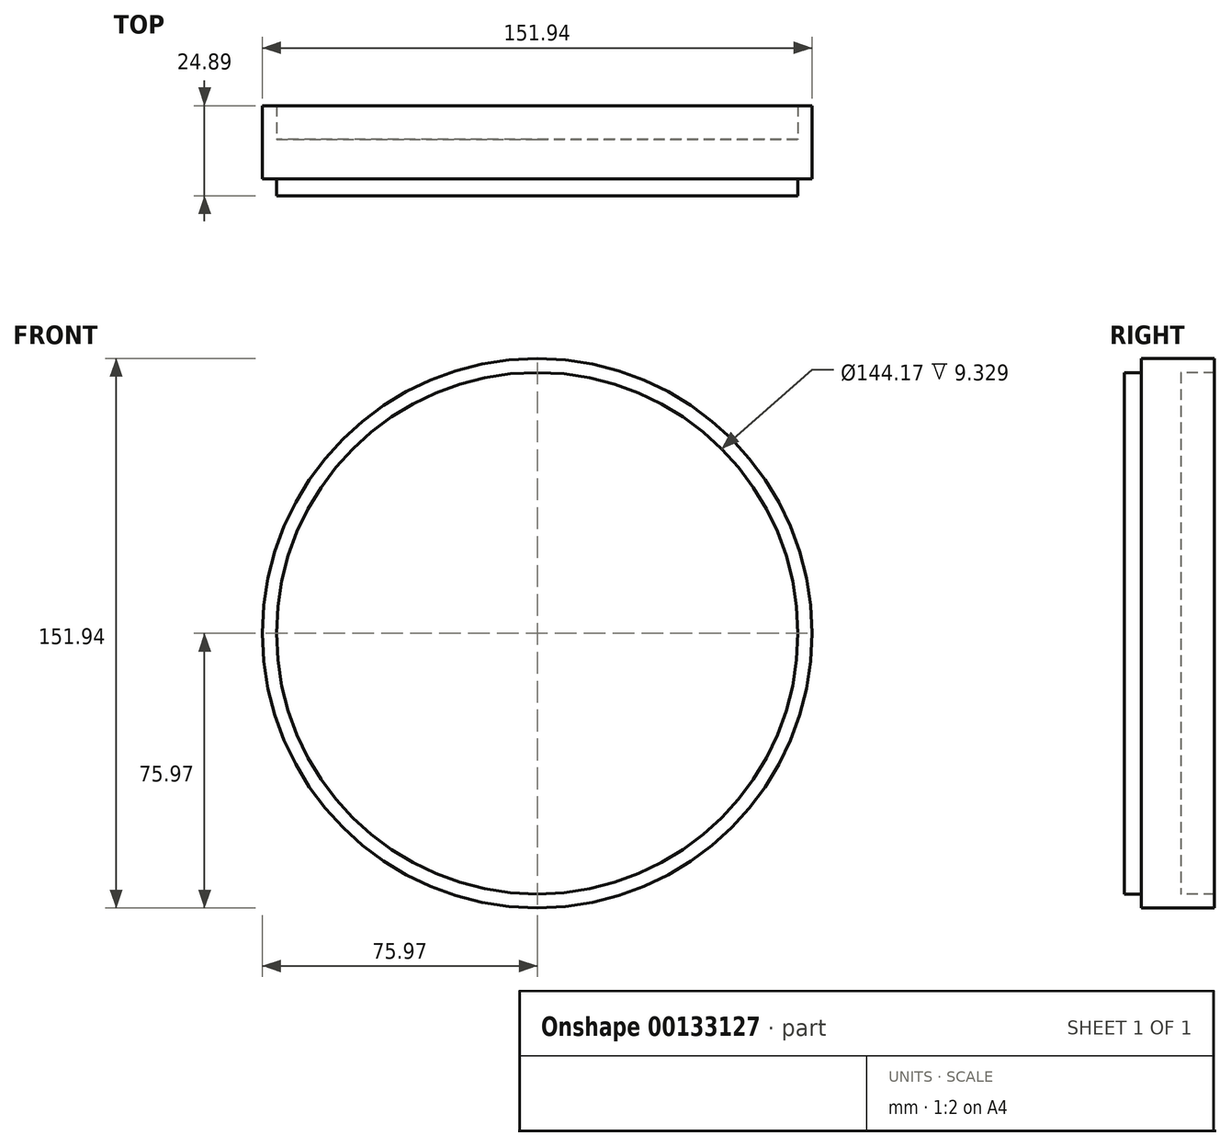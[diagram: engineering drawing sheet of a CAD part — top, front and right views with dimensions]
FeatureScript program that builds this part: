
annotation { "Feature Type Name" : "Feature", "Feature Type Description" : "" }
export const myFeature = defineFeature(function(context is Context, id is Id, definition is map)
    precondition{}
    {
        {
            var Q0;
            Q0=qCreatedBy(makeId("Front.planeOp"),FACE);
            var sketch = newSketch(context, id + "F0", { "sketchPlane" : qUnion([Q0])});
            skCircle(sketch, "E0", {"center": v(0, 0) * mm, "radius": 75.97 * mm});
            skCircle(sketch, "E1", {"center": v(0, 0) * mm, "radius": 70.64 * mm});
            skSolve(sketch);
        }
        {
            var Q0;
            Q0=makeQuery(id+"F0.imprint","IMPRINT",FACE,{"disambiguationData":[TD([[makeQuery(id+"F0.imprint","IMPRINT",EDGE,{"derivedFrom":sQuery(id+"F0.wireOp",EDGE,"E0")}),1.0]])]});
            extrude(context, id + "F1", {"entities" : qUnion([Q0]), "depth" : 10.9 * mm});
        }
        {
            var Q0;
            Q0=qCreatedBy(makeId("Front.planeOp"),FACE);
            var sketch = newSketch(context, id + "F2", { "sketchPlane" : qUnion([Q0])});
            skCircle(sketch, "E2", {"center": v(0, 0) * mm, "radius": 72.1 * mm});
            skSolve(sketch);
        }
        {
            var Q0;
            Q0=makeQuery(id+"F2.imprint","IMPRINT",FACE,{"disambiguationData":[TD([[makeQuery(id+"F2.imprint","IMPRINT",EDGE,{"derivedFrom":sQuery(id+"F2.wireOp",EDGE,"E2")}),1.0]])]});
            extrude(context, id + "F3", {"entities" : qUnion([Q0]), "operationType" : NewBodyOperationType.ADD, "depth" : 15.56 * mm});
        }
        {
            var Q0;
            Q0=makeQuery(id+"F3.boolean.opBoolean","MERGE",FACE,{"derivedFrom":[makeQuery(id+"F1.opExtrude","CAP_FACE",FACE,{"disambiguationData":[OSD([sQuery(id+"F0.wireOp",EDGE,"E0"),sQuery(id+"F0.wireOp",EDGE,"E1")])],"isStart":true}),makeQuery(id+"F3.opExtrude","CAP_FACE",FACE,{"disambiguationData":[OSD([sQuery(id+"F2.wireOp",EDGE,"E2")])],"isStart":true})]});
            var sketch = newSketch(context, id + "F4", { "sketchPlane" : qUnion([Q0])});
            skCircle(sketch, "E3", {"center": v(0, 0) * mm, "radius": 72.09 * mm});
            skSolve(sketch);
        }
        {
            var Q0;
            Q0=makeQuery(id+"F4.imprint","IMPRINT",FACE,{"disambiguationData":[TD([[makeQuery(id+"F4.imprint","IMPRINT",EDGE,{"derivedFrom":sQuery(id+"F4.wireOp",EDGE,"E3")}),-1.0]])]});
            extrude(context, id + "F5", {"entities" : qUnion([Q0]), "operationType" : NewBodyOperationType.ADD, "depth" : 9.33 * mm});
        }
    });
